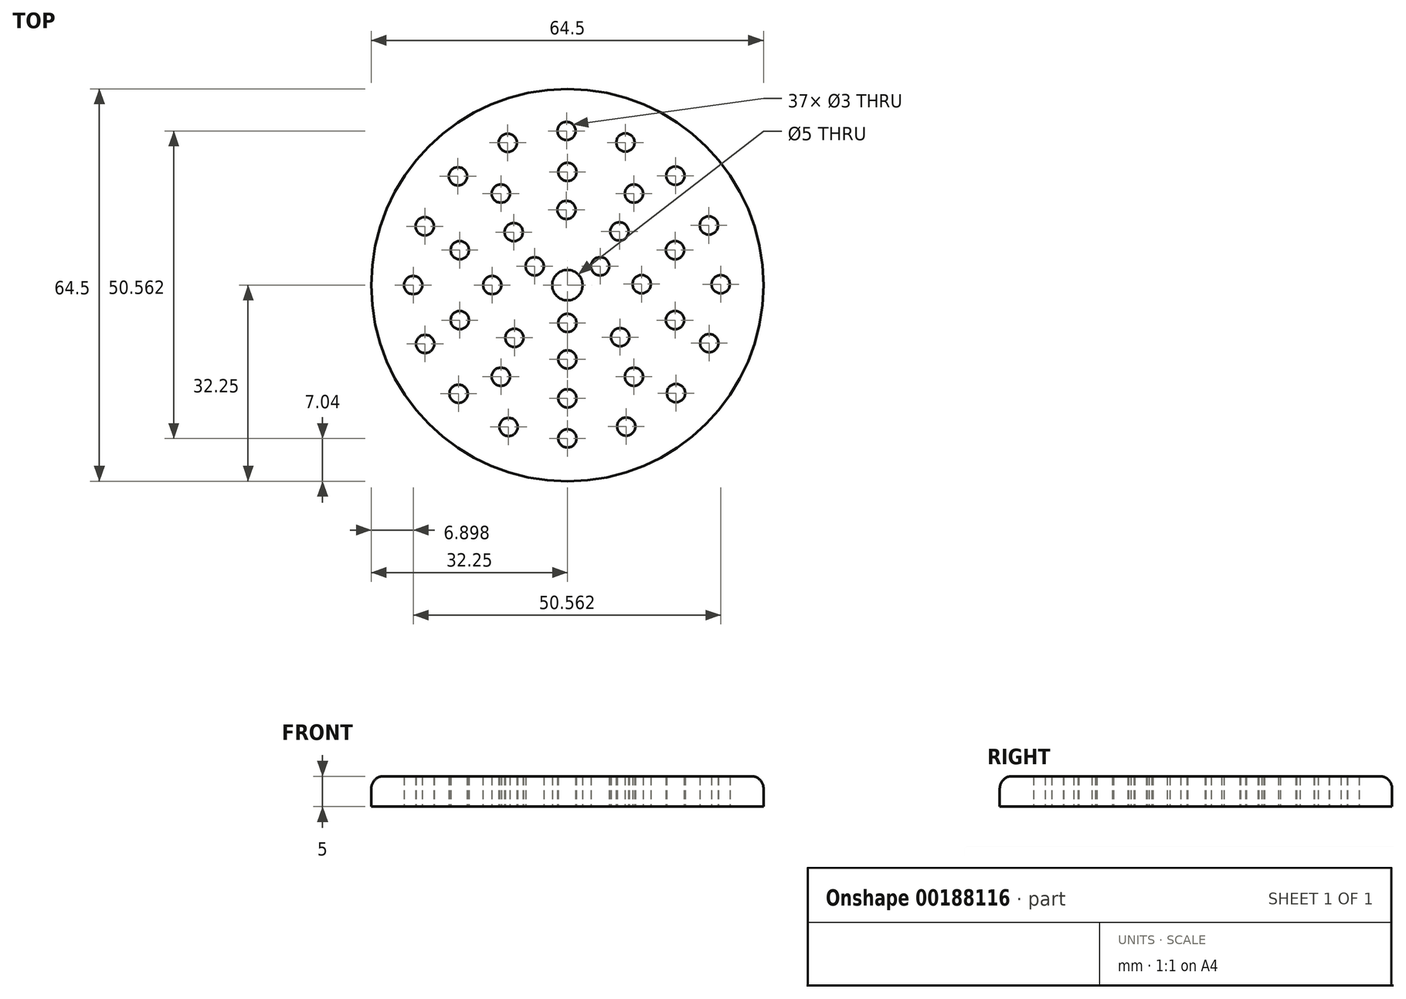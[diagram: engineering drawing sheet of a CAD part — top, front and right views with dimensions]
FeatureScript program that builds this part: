
annotation { "Feature Type Name" : "Feature", "Feature Type Description" : "" }
export const myFeature = defineFeature(function(context is Context, id is Id, definition is map)
    precondition{}
    {
        {
            var Q0;
            Q0=qCreatedBy(makeId("Top.planeOp"),FACE);
            var sketch = newSketch(context, id + "F0", { "sketchPlane" : qUnion([Q0])});
            skCircle(sketch, "E0", {"center": v(0, 0) * mm, "radius": 32.25 * mm});
            skCircle(sketch, "E1", {"center": v(-25.35, 0) * mm, "radius": 1.5 * mm});
            skCircle(sketch, "E2.1.0", {"center": v(-23.4, -9.67) * mm, "radius": 1.5 * mm});
            skCircle(sketch, "E2.2.0", {"center": v(-17.9, -17.86) * mm, "radius": 1.5 * mm});
            skCircle(sketch, "E2.3.0", {"center": v(-9.68, -23.31) * mm, "radius": 1.5 * mm});
            skCircle(sketch, "E2.4.0", {"center": v(0, -25.21) * mm, "radius": 1.5 * mm});
            skCircle(sketch, "E2.5.0", {"center": v(9.67, -23.26) * mm, "radius": 1.5 * mm});
            skCircle(sketch, "E2.6.0", {"center": v(17.86, -17.76) * mm, "radius": 1.5 * mm});
            skCircle(sketch, "E2.7.0", {"center": v(23.31, -9.54) * mm, "radius": 1.5 * mm});
            skCircle(sketch, "E2.8.0", {"center": v(25.21, 0.14) * mm, "radius": 1.5 * mm});
            skCircle(sketch, "E2.9.0", {"center": v(23.26, 9.81) * mm, "radius": 1.5 * mm});
            skCircle(sketch, "E2.10.0", {"center": v(17.76, 18) * mm, "radius": 1.5 * mm});
            skCircle(sketch, "E2.11.0", {"center": v(9.54, 23.45) * mm, "radius": 1.5 * mm});
            skCircle(sketch, "E2.12.0", {"center": v(-0.14, 25.35) * mm, "radius": 1.5 * mm});
            skCircle(sketch, "E2.13.0", {"center": v(-9.81, 23.4) * mm, "radius": 1.5 * mm});
            skCircle(sketch, "E2.14.0", {"center": v(-18, 17.9) * mm, "radius": 1.5 * mm});
            skCircle(sketch, "E2.15.0", {"center": v(-23.45, 9.68) * mm, "radius": 1.5 * mm});
            skPoint(sketch, "E2.center", {"position": v(-0.07, 0.07) * mm});
            skCircle(sketch, "E3", {"center": v(-12.37, 0) * mm, "radius": 1.5 * mm});
            skCircle(sketch, "E4.1.0", {"center": v(-8.71, -8.67) * mm, "radius": 1.5 * mm});
            skCircle(sketch, "E4.2.0", {"center": v(0, -12.21) * mm, "radius": 1.5 * mm});
            skCircle(sketch, "E4.3.0", {"center": v(8.67, -8.55) * mm, "radius": 1.5 * mm});
            skCircle(sketch, "E4.4.0", {"center": v(12.21, 0.16) * mm, "radius": 1.5 * mm});
            skCircle(sketch, "E4.5.0", {"center": v(8.55, 8.82) * mm, "radius": 1.5 * mm});
            skCircle(sketch, "E4.6.0", {"center": v(-0.16, 12.37) * mm, "radius": 1.5 * mm});
            skCircle(sketch, "E4.7.0", {"center": v(-8.82, 8.71) * mm, "radius": 1.5 * mm});
            skPoint(sketch, "E4.center", {"position": v(-0.08, 0.08) * mm});
            skCircle(sketch, "E5", {"center": v(0, 0) * mm, "radius": 2.5 * mm});
            skCircle(sketch, "E6", {"center": v(0, -18.61) * mm, "radius": 1.5 * mm});
            skCircle(sketch, "E7.1.0", {"center": v(10.94, -15.06) * mm, "radius": 1.5 * mm});
            skCircle(sketch, "E7.2.0", {"center": v(17.7, -5.75) * mm, "radius": 1.5 * mm});
            skCircle(sketch, "E8.1.3.0", {"center": v(17.7, 5.75) * mm, "radius": 1.5 * mm});
            skCircle(sketch, "E8.1.4.0", {"center": v(10.94, 15.06) * mm, "radius": 1.5 * mm});
            skCircle(sketch, "E8.1.5.0", {"center": v(0, 18.61) * mm, "radius": 1.5 * mm});
            skCircle(sketch, "E8.1.6.0", {"center": v(-10.94, 15.06) * mm, "radius": 1.5 * mm});
            skCircle(sketch, "E8.1.7.0", {"center": v(-17.7, 5.75) * mm, "radius": 1.5 * mm});
            skCircle(sketch, "E8.1.8.0", {"center": v(-17.7, -5.75) * mm, "radius": 1.5 * mm});
            skCircle(sketch, "E8.1.9.0", {"center": v(-10.94, -15.06) * mm, "radius": 1.5 * mm});
            skCircle(sketch, "E9", {"center": v(0, -6.21) * mm, "radius": 1.5 * mm});
            skCircle(sketch, "E10.1.0", {"center": v(5.38, 3.1) * mm, "radius": 1.5 * mm});
            skCircle(sketch, "E10.2.0", {"center": v(-5.38, 3.1) * mm, "radius": 1.5 * mm});
            skSolve(sketch);
        }
        {
            var Q0;
            Q0=makeQuery(id+"F0.imprint","IMPRINT",FACE,{"disambiguationData":[TD([[makeQuery(id+"F0.imprint","IMPRINT",EDGE,{"derivedFrom":sQuery(id+"F0.wireOp",EDGE,"E0")}),1.0]])]});
            extrude(context, id + "F1", {"entities" : qUnion([Q0]), "depth" : 5 * mm});
        }
        {
            var Q0;
            Q0=makeQuery(id+"F1.opExtrude","CAP_EDGE",EDGE,{"disambiguationData":[OSD([sQuery(id+"F0.wireOp",EDGE,"E0")])],"isStart":false});
            fillet(context, id + "F2", {"entities" : qUnion([Q0]), "radius" : 2 * mm, "tangentPropagation" : true, "allowEdgeOverflow" : false});
        }
    });
